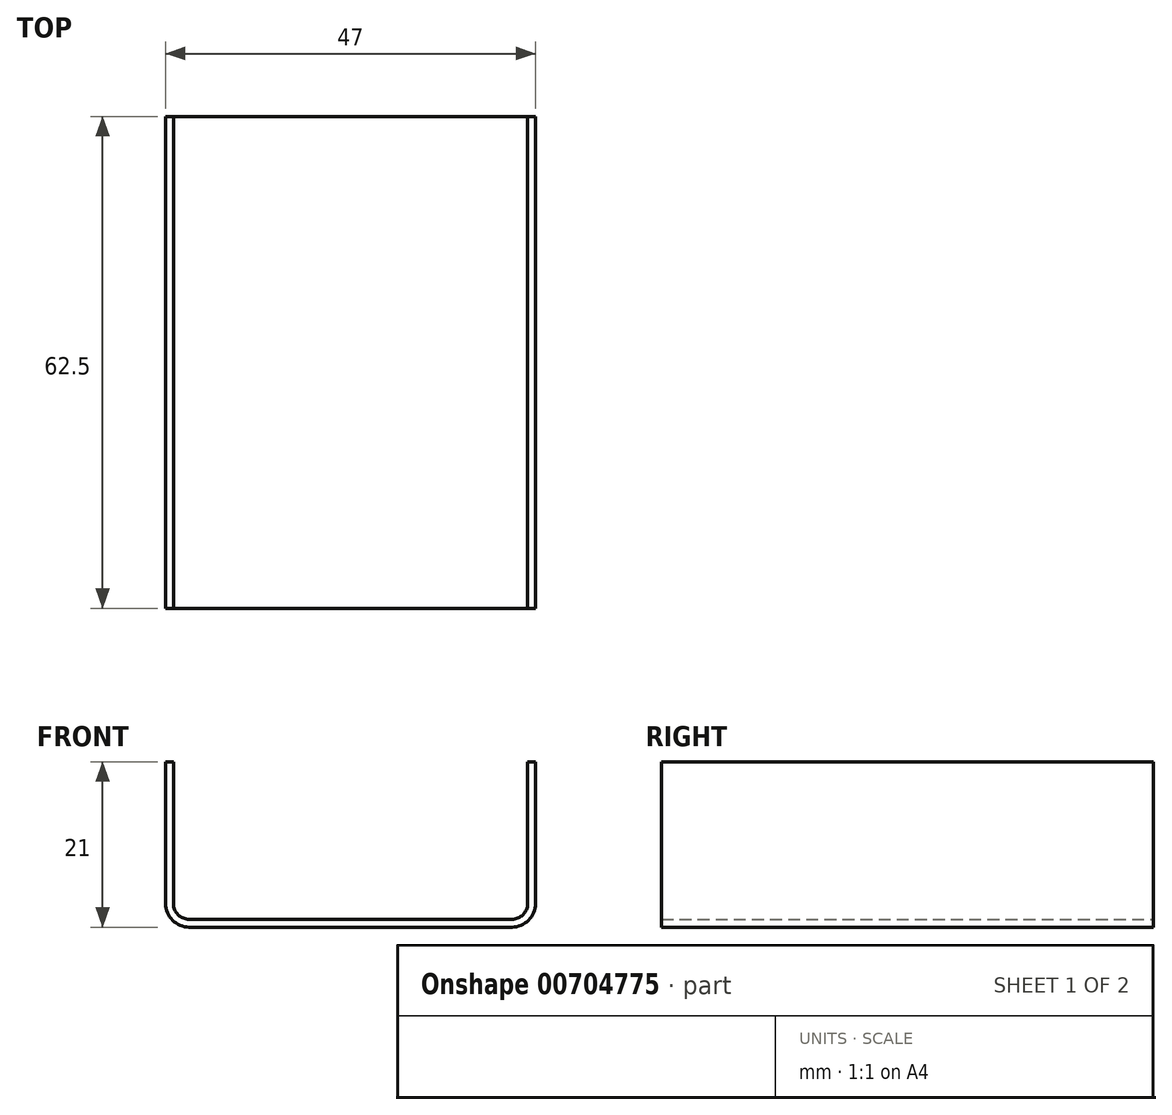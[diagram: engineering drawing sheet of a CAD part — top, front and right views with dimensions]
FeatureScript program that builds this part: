
annotation { "Feature Type Name" : "Feature", "Feature Type Description" : "" }
export const myFeature = defineFeature(function(context is Context, id is Id, definition is map)
    precondition{}
    {
        {
            var Q0;
            Q0=qCreatedBy(makeId("Top.planeOp"),FACE);
            var sketch = newSketch(context, id + "F0", { "sketchPlane" : qUnion([Q0])});
            skLineSegment(sketch, "E0.bottom", {"start": v(23.5, -31.25) * mm, "end": v(-23.5, -31.25) * mm});
            skLineSegment(sketch, "E0.top", {"start": v(23.5, 31.25) * mm, "end": v(-23.5, 31.25) * mm});
            skLineSegment(sketch, "E0.left", {"start": v(23.5, -31.25) * mm, "end": v(23.5, 31.25) * mm});
            skLineSegment(sketch, "E0.right", {"start": v(-23.5, -31.25) * mm, "end": v(-23.5, 31.25) * mm});
            skPoint(sketch, "E0.middle", {"position": v(0, 0) * mm});
            skSolve(sketch);
        }
        {
            var Q0;
            Q0 = qSketchRegion(id + "F0", true);
            extrude(context, id + "F1", {"entities" : qUnion([Q0]), "depth" : 21 * mm, "offsetDistance" : 25 * mm});
        }
        {
            var Q0;
            Q0=makeQuery(id+"F1.opExtrude","CAP_EDGE",EDGE,{"disambiguationData":[OSD([sQuery(id+"F0.wireOp",EDGE,"E0.left")])],"isStart":true});
            var Q1;
            Q1=makeQuery(id+"F1.opExtrude","CAP_EDGE",EDGE,{"disambiguationData":[OSD([sQuery(id+"F0.wireOp",EDGE,"E0.right")])],"isStart":true});
            fillet(context, id + "F2", {"entities" : qUnion([Q0, Q1]), "radius" : 3 * mm, "tangentPropagation" : true, "allowEdgeOverflow" : false});
        }
        {
            var Q0;
            Q0=makeQuery(id+"F1.opExtrude","CAP_FACE",FACE,{"disambiguationData":[OSD([sQuery(id+"F0.wireOp",EDGE,"E0.bottom"),sQuery(id+"F0.wireOp",EDGE,"E0.top"),sQuery(id+"F0.wireOp",EDGE,"E0.left"),sQuery(id+"F0.wireOp",EDGE,"E0.right")])],"isStart":false});
            var Q1;
            Q1=makeQuery(id+"F1.opExtrude","SWEPT_FACE",FACE,{"disambiguationData":[OSD([sQuery(id+"F0.wireOp",EDGE,"E0.bottom")])]});
            var Q2;
            Q2=makeQuery(id+"F1.opExtrude","SWEPT_FACE",FACE,{"disambiguationData":[OSD([sQuery(id+"F0.wireOp",EDGE,"E0.top")])]});
            shell(context, id + "F3", {"entities" : qUnion([Q0, Q1, Q2]), "thickness" : 1 * mm});
        }
    });
